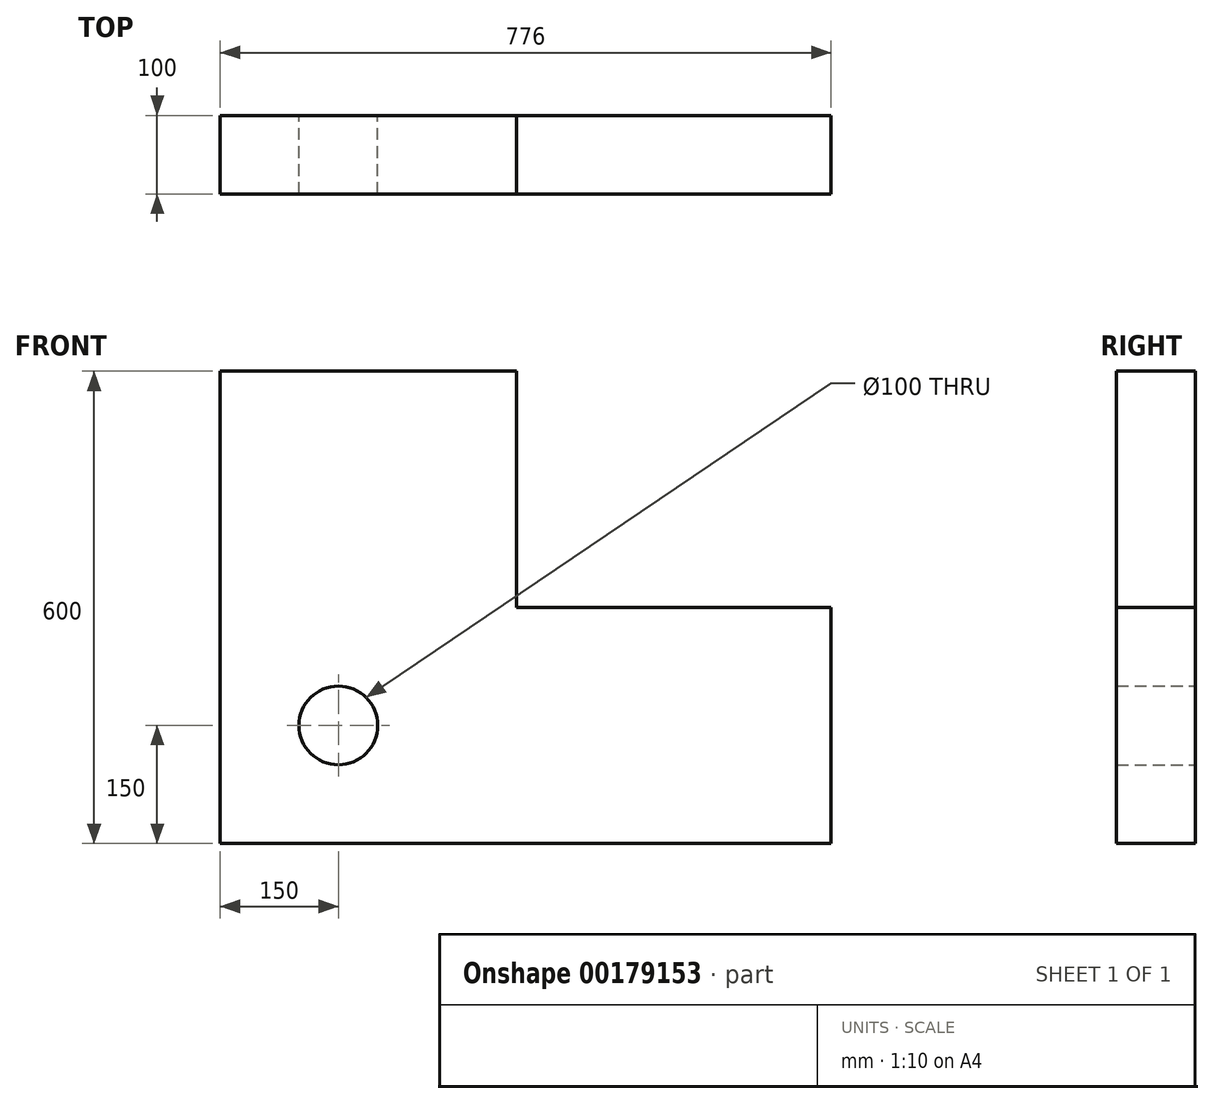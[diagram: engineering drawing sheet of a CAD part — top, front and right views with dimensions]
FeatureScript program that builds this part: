
annotation { "Feature Type Name" : "Feature", "Feature Type Description" : "" }
export const myFeature = defineFeature(function(context is Context, id is Id, definition is map)
    precondition{}
    {
        {
            var Q0;
            Q0=qCreatedBy(makeId("Front.planeOp"),FACE);
            var sketch = newSketch(context, id + "F0", { "sketchPlane" : qUnion([Q0])});
            skLineSegment(sketch, "E0", {"start": v(0, 0) * mm, "end": v(776, 0) * mm});
            skLineSegment(sketch, "E1", {"start": v(776, 0) * mm, "end": v(776, 300) * mm});
            skLineSegment(sketch, "E2", {"start": v(776, 300) * mm, "end": v(376, 300) * mm});
            skLineSegment(sketch, "E3", {"start": v(376, 300) * mm, "end": v(376, 600) * mm});
            skLineSegment(sketch, "E4", {"start": v(376, 600) * mm, "end": v(0, 600) * mm});
            skLineSegment(sketch, "E5", {"start": v(0, 600) * mm, "end": v(0, 0) * mm});
            skCircle(sketch, "E6", {"center": v(150, 150) * mm, "radius": 50 * mm});
            skSolve(sketch);
        }
        {
            var Q0;
            Q0=makeQuery(id+"F0.imprint","IMPRINT",FACE,{"disambiguationData":[TD([[makeQuery(id+"F0.imprint","IMPRINT",EDGE,{"derivedFrom":sQuery(id+"F0.wireOp",EDGE,"E0")}),1.0]])]});
            extrude(context, id + "F1", {"entities" : qUnion([Q0]), "depth" : 100 * mm});
        }
    });
